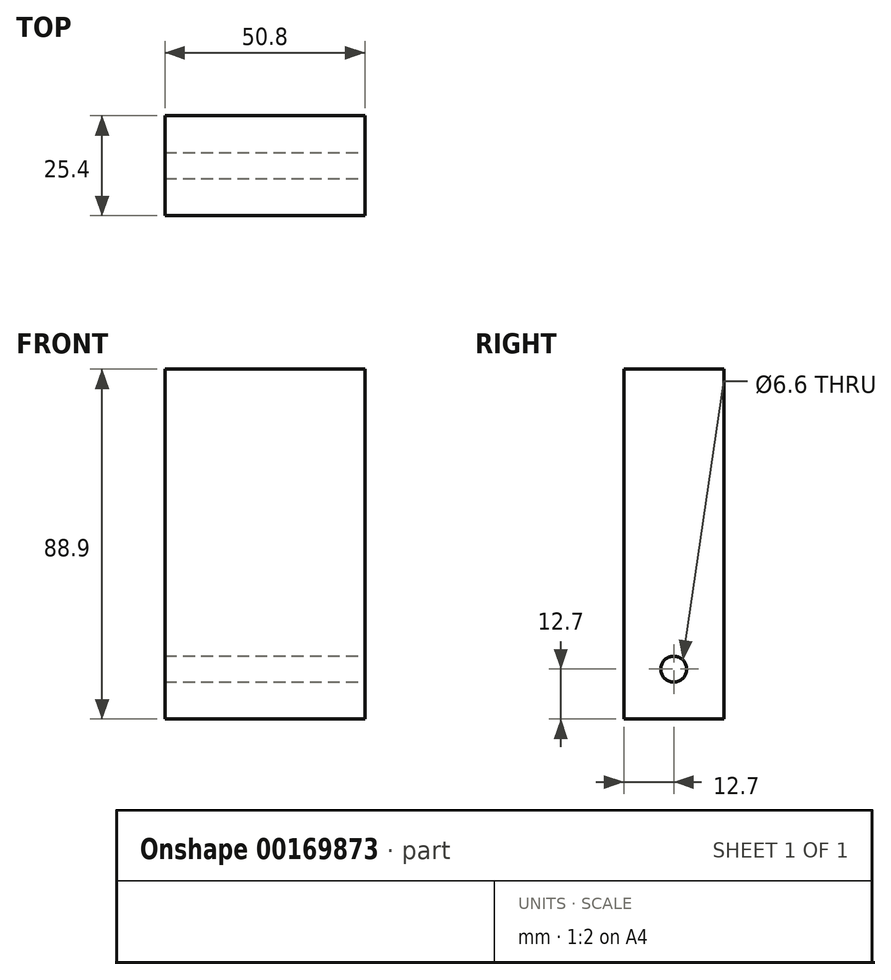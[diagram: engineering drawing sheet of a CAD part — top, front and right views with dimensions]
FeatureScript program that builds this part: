
annotation { "Feature Type Name" : "Feature", "Feature Type Description" : "" }
export const myFeature = defineFeature(function(context is Context, id is Id, definition is map)
    precondition{}
    {
        {
            var Q0;
            Q0=qCreatedBy(makeId("Front.planeOp"),FACE);
            var sketch = newSketch(context, id + "F0", { "sketchPlane" : qUnion([Q0])});
            skLineSegment(sketch, "E0.bottom", {"start": v(-25.4, -44.45) * mm, "end": v(25.4, -44.45) * mm});
            skLineSegment(sketch, "E0.top", {"start": v(-25.4, 44.45) * mm, "end": v(25.4, 44.45) * mm});
            skLineSegment(sketch, "E0.left", {"start": v(-25.4, -44.45) * mm, "end": v(-25.4, 44.45) * mm});
            skLineSegment(sketch, "E0.right", {"start": v(25.4, -44.45) * mm, "end": v(25.4, 44.45) * mm});
            skPoint(sketch, "E0.middle", {"position": v(0, 0) * mm});
            skSolve(sketch);
        }
        {
            var Q0;
            Q0=makeQuery(id+"F0.imprint","IMPRINT",FACE,{"disambiguationData":[TD([[makeQuery(id+"F0.imprint","IMPRINT",EDGE,{"derivedFrom":sQuery(id+"F0.wireOp",EDGE,"E0.bottom")}),1.0]])]});
            extrude(context, id + "F1", {"entities" : qUnion([Q0]), "depth" : 25.4 * mm});
        }
        {
            var Q0;
            Q0=makeQuery(id+"F1.opExtrude","SWEPT_FACE",FACE,{"disambiguationData":[OSD([sQuery(id+"F0.wireOp",EDGE,"E0.right")])]});
            var sketch = newSketch(context, id + "F2", { "sketchPlane" : qUnion([Q0])});
            skLineSegment(sketch, "E1", {"start": v(-12.7, -44.45) * mm, "end": v(-12.7, -31.75) * mm, "construction": true});
            skCircle(sketch, "E2", {"center": v(-12.7, -31.75) * mm, "radius": 3.3 * mm});
            skSolve(sketch);
        }
        {
            var Q0;
            Q0=makeQuery(id+"F2.imprint","IMPRINT",FACE,{"disambiguationData":[TD([[makeQuery(id+"F2.imprint","IMPRINT",EDGE,{"derivedFrom":sQuery(id+"F2.wireOp",EDGE,"E2")}),1.0]])]});
            extrude(context, id + "F3", {"entities" : qUnion([Q0]), "operationType" : NewBodyOperationType.REMOVE, "endBound" : BoundingType.THROUGH_ALL, "oppositeDirection" : true, "depth" : 25.4 * mm});
        }
    });
